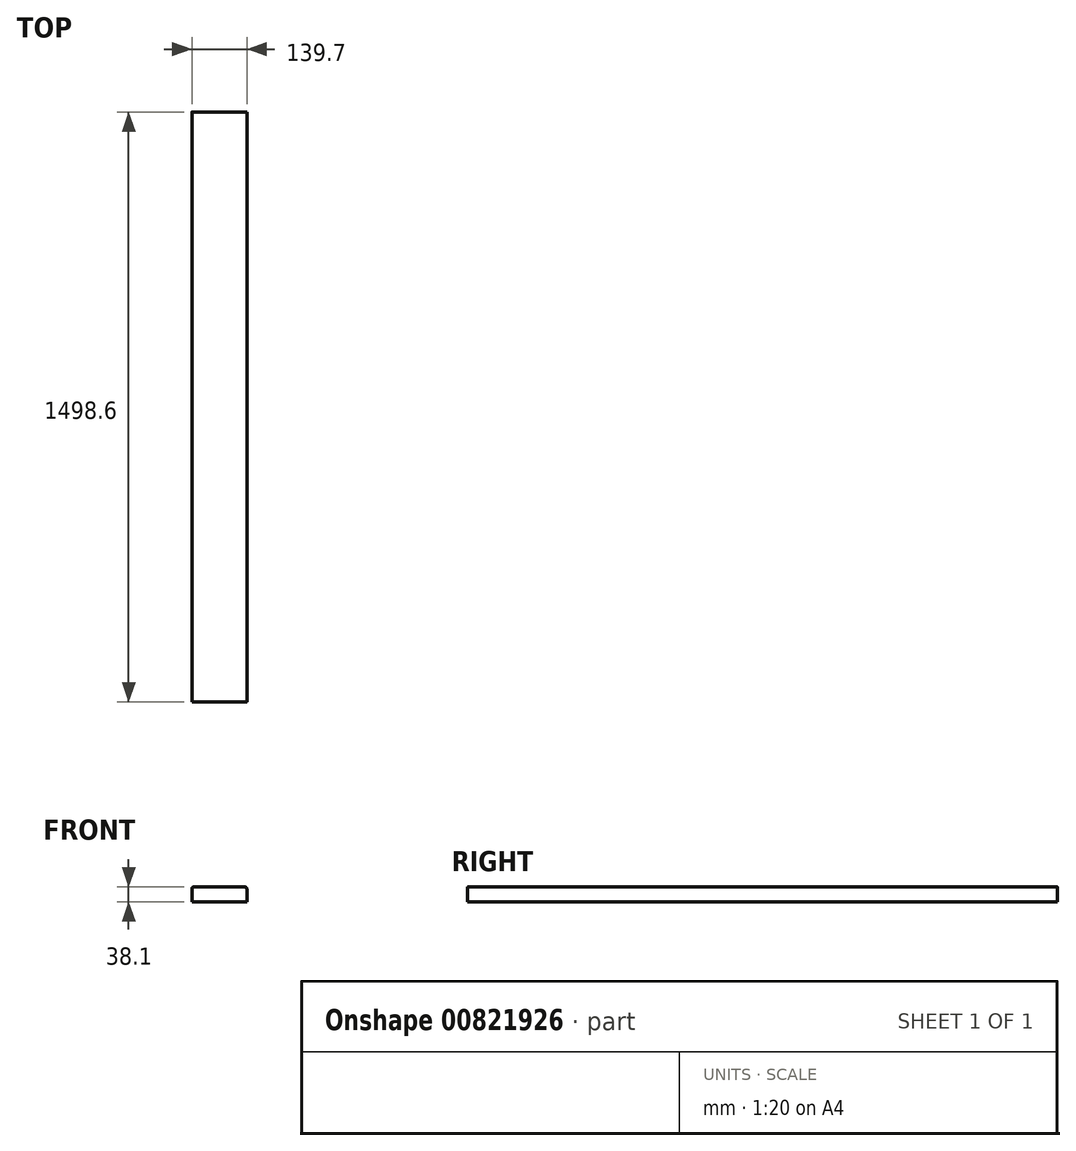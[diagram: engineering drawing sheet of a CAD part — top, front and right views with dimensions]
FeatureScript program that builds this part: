
annotation { "Feature Type Name" : "Feature", "Feature Type Description" : "" }
export const myFeature = defineFeature(function(context is Context, id is Id, definition is map)
    precondition{}
    {
        {
            var Q0;
            Q0=qCreatedBy(makeId("Top.planeOp"),FACE);
            var sketch = newSketch(context, id + "F0", { "sketchPlane" : qUnion([Q0])});
            skLineSegment(sketch, "E0.bottom", {"start": v(0, 0) * mm, "end": v(139.7, 0) * mm});
            skLineSegment(sketch, "E0.top", {"start": v(0, 1498.6) * mm, "end": v(139.7, 1498.6) * mm});
            skLineSegment(sketch, "E0.left", {"start": v(0, 0) * mm, "end": v(0, 1498.6) * mm});
            skLineSegment(sketch, "E0.right", {"start": v(139.7, 0) * mm, "end": v(139.7, 1498.6) * mm});
            skSolve(sketch);
        }
        {
            var Q0;
            Q0=makeQuery(id+"F0.imprint","IMPRINT",FACE,{"disambiguationData":[TD([[makeQuery(id+"F0.imprint","IMPRINT",EDGE,{"derivedFrom":sQuery(id+"F0.wireOp",EDGE,"E0.bottom")}),1.0]])]});
            extrude(context, id + "F1", {"entities" : qUnion([Q0]), "depth" : 38.1 * mm, "offsetDistance" : 25.4 * mm});
        }
        {
            var Q0;
            Q0=makeQuery(id+"F1.opExtrude","CAP_EDGE",EDGE,{"disambiguationData":[OSD([sQuery(id+"F0.wireOp",EDGE,"E0.left")])],"isStart":false});
            var Q1;
            Q1=makeQuery(id+"F1.opExtrude","CAP_EDGE",EDGE,{"disambiguationData":[OSD([sQuery(id+"F0.wireOp",EDGE,"E0.right")])],"isStart":false});
            fillet(context, id + "F2", {"entities" : qUnion([Q0, Q1]), "radius" : 5.08 * mm, "tangentPropagation" : true, "allowEdgeOverflow" : false});
        }
    });
